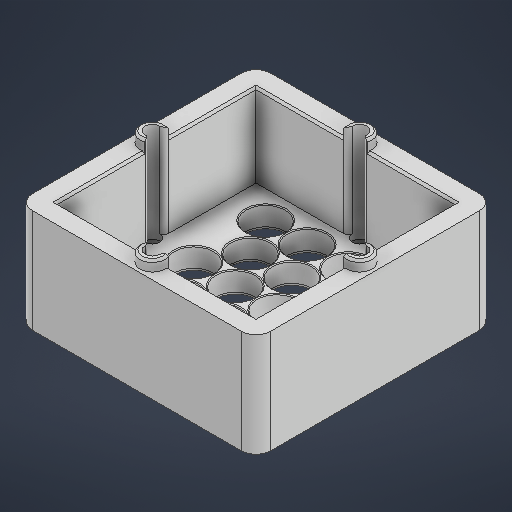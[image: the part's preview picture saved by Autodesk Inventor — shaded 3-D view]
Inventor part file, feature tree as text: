
AUTODESK INVENTOR PART (.ipt)
format: ipt  version: 2025 (Build 290162000, 162)  size: 432,128 bytes
history: native  units: in
note: dims shown in document units (in); Inventor stores cm internally (conversion verified against a paired STEP export)
features: sketch x7, extrude x3, hole x2, fillet x2, chamfer x2
ambient origin geometry x8: Origin, YZ Plane, XZ Plane, XY Plane, X Axis, Y Axis, Z Axis, Center Point
bodies: Solid1 (feature_tree)
feature tree (16):
  extrude  "Extrusion1"  Depth=4.5276in
  sketch  "Sketch4"  dims[d2=0.3937in d3=0.0in d48=3.7795in]
  extrude  "Extrusion3"  Depth=3.7795in
  hole  "Hole4"  [1 undecoded]
  hole  "Hole5"  [1 undecoded]
  extrude  "Extrusion4"  Depth=1.5748in
  fillet  "Fillet1"  Radius=0.748in
  fillet  "Fillet2"  Radius=0.3937in
  chamfer  "Chamfer1"  Distance=1.5748in
  chamfer  "Chamfer2"  Distance=3.937in
  sketch  "Sketch1"  dims[d0=4.5276in d1=4.5276in]
  sketch  "Sketch Rectangular Pattern11"  dims[d134=0.748in d135=1.5748in d137=0.7874in d138=1.1811in d140=1.3638in d143=0.748in d146=0.3937in]
  sketch  "Sketch Rectangular Pattern12"  dims[d147=0.6819in]
  sketch  "Sketch6"  dims[d49=3.7795in d124=1.3638in]
  sketch  "Sketch Rectangular Pattern14"  dims[d148=1.1811in d150=0.7874in d151=0.7874in d153=1.3638in d174=1.5748in d175=0.0in d176=0.7323in d177=0.2362in d178=0.748in d179=0.0787in d180=0.0172in d181=0.315in d182=0.8108in d183=3.937in d184=3.937in d185=0.2362in d186=1.1811in d188=1.9685in d189=1.1811in d191=1.9685in d194=0.2805in d195=0.2362in d196=0.5118in d197=0.2756in d198=0.0172in d199=0.315in d200=0.8108in d201=0.4724in d202=0.4724in d203=0.4724in d204=0.4724in d205=0.1969in d206=0.0in d207=0.2805in d208=0.0787in d209=0.0157in d210=0.0787in d211=45.0deg d212=0.0394in d213=0.0787in d214=45.0deg]
  sketch  "Sketch7"  dims[d132=2.3622in d133=2.7276in]
note: 2 required parameter values undecoded (feature->parameter linkage not recoverable at this tier; creation-order binding heuristic only, values carry confidence <= 0.55)
